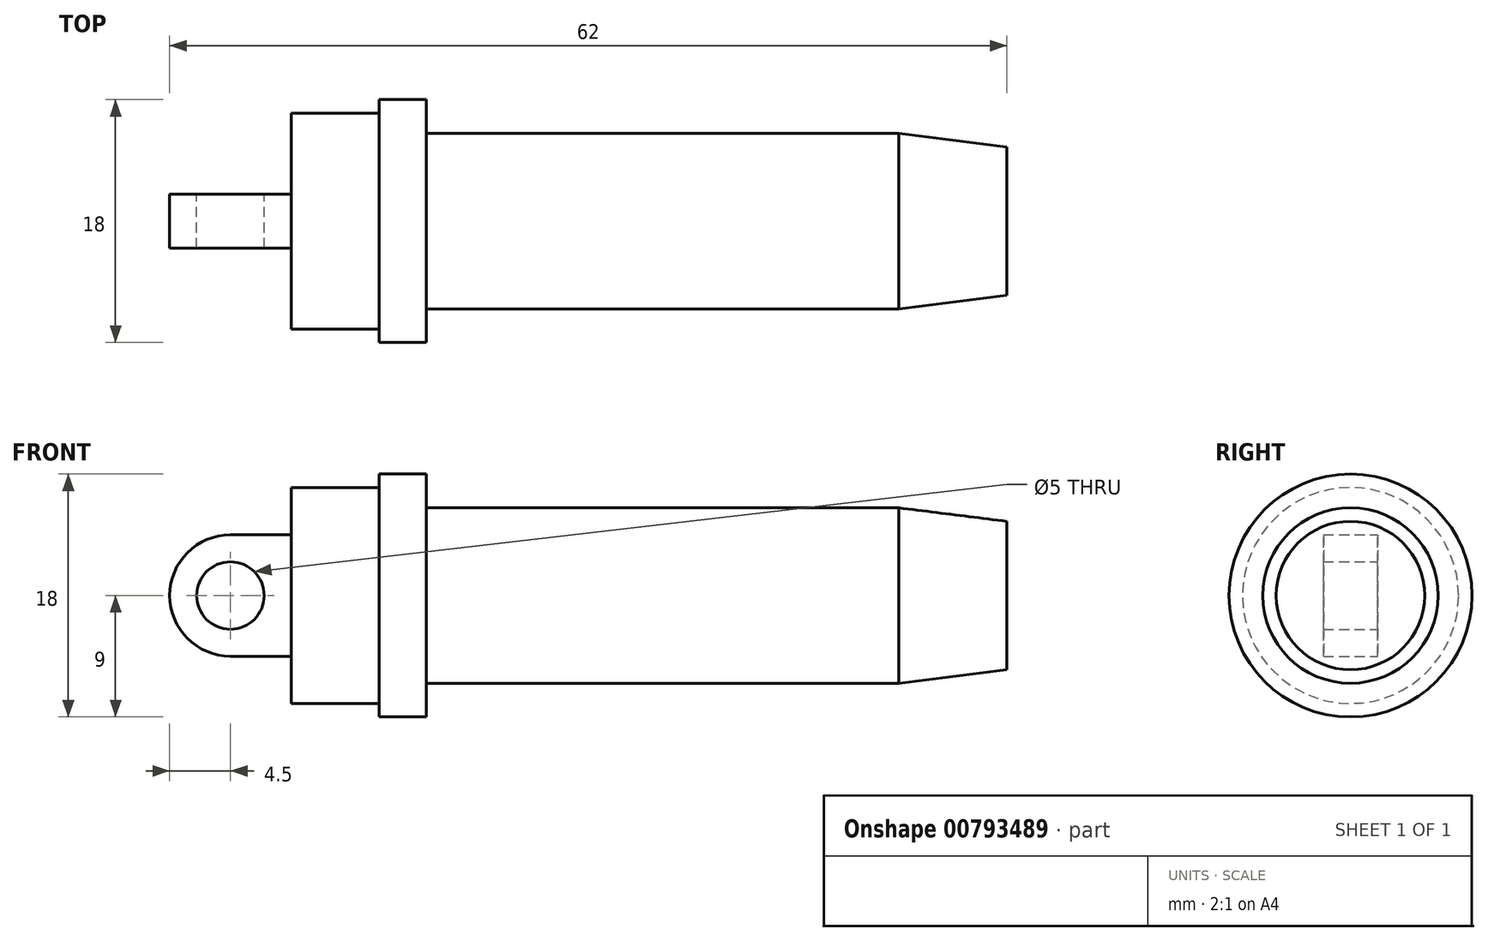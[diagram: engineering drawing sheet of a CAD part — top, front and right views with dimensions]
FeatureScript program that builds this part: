
annotation { "Feature Type Name" : "Feature", "Feature Type Description" : "" }
export const myFeature = defineFeature(function(context is Context, id is Id, definition is map)
    precondition{}
    {
        {
            var Q0;
            Q0=qCreatedBy(makeId("Front.planeOp"),FACE);
            var sketch = newSketch(context, id + "F0", { "sketchPlane" : qUnion([Q0])});
            skCircle(sketch, "E0", {"center": v(0, 0) * mm, "radius": 2.5 * mm});
            skArc(sketch, "E1", {"start": v(0, 4.5) * mm, "mid": v(-4.5, 0) * mm, "end": v(0, -4.5) * mm});
            skLineSegment(sketch, "E2", {"start": v(0, 4.5) * mm, "end": v(4.5, 4.5) * mm});
            skLineSegment(sketch, "E3", {"start": v(0, -4.5) * mm, "end": v(4.5, -4.5) * mm});
            skLineSegment(sketch, "E4", {"start": v(4.5, -4.5) * mm, "end": v(4.5, 4.5) * mm});
            skLineSegment(sketch, "E5", {"start": v(4.5, 4.5) * mm, "end": v(4.5, 8) * mm});
            skLineSegment(sketch, "E6", {"start": v(4.5, 8) * mm, "end": v(11, 8) * mm});
            skLineSegment(sketch, "E7", {"start": v(11, 8) * mm, "end": v(11, 9) * mm});
            skLineSegment(sketch, "E8", {"start": v(11, 9) * mm, "end": v(14.5, 9) * mm});
            skLineSegment(sketch, "E9", {"start": v(14.5, 9) * mm, "end": v(14.5, 6.5) * mm});
            skLineSegment(sketch, "E10", {"start": v(14.5, 6.5) * mm, "end": v(49.5, 6.5) * mm});
            skLineSegment(sketch, "E11", {"start": v(49.5, 6.5) * mm, "end": v(57.5, 5.5) * mm});
            skLineSegment(sketch, "E12", {"start": v(4.5, 0) * mm, "end": v(57.5, 0) * mm});
            skLineSegment(sketch, "E13", {"start": v(57.5, 5.5) * mm, "end": v(57.5, 0) * mm});
            skSolve(sketch);
        }
        {
            var Q0;
            Q0=makeQuery(id+"F0.imprint","IMPRINT",FACE,{"disambiguationData":[TD([[makeQuery(id+"F0.imprint","IMPRINT",EDGE,{"derivedFrom":sQuery(id+"F0.wireOp",EDGE,"E0")}),-1.0]])]});
            var Q1;
            Q1=makeQuery(id+"F0.imprint","IMPRINT",FACE,{"disambiguationData":[TD([[makeQuery(id+"F0.imprint","IMPRINT",EDGE,{"derivedFrom":sQuery(id+"F0.wireOp",EDGE,"neKaYsiq-PykI-cqrg-KBEg-4rQ8FbIlcUME")}),-1.0]])]});
            extrude(context, id + "F1", {"entities" : qUnion([Q0, Q1]), "endBound" : BoundingType.SYMMETRIC, "depth" : 4 * mm, "offsetDistance" : 25 * mm});
        }
        {
            var Q0;
            {var subQ0=sQuery(id+"F0.wireOp",EDGE,"E5");Q0=makeQuery(id+"F0.imprint","IMPRINT",FACE,{"disambiguationData":[TD([[makeQuery(id+"F0.imprint","IMPRINT",EDGE,{"derivedFrom":subQ0}),-1.0]])]});}
            var Q1;
            Q1=sQuery(id+"F0.wireOp",EDGE,"E12");
            revolve(context, id + "F2", {"operationType" : NewBodyOperationType.ADD, "surfaceOperationType" : NewSurfaceOperationType.NEW, "entities" : qUnion([Q0]), "axis" : qUnion([Q1]), "revolveType" : RevolveType.FULL});
        }
    });
